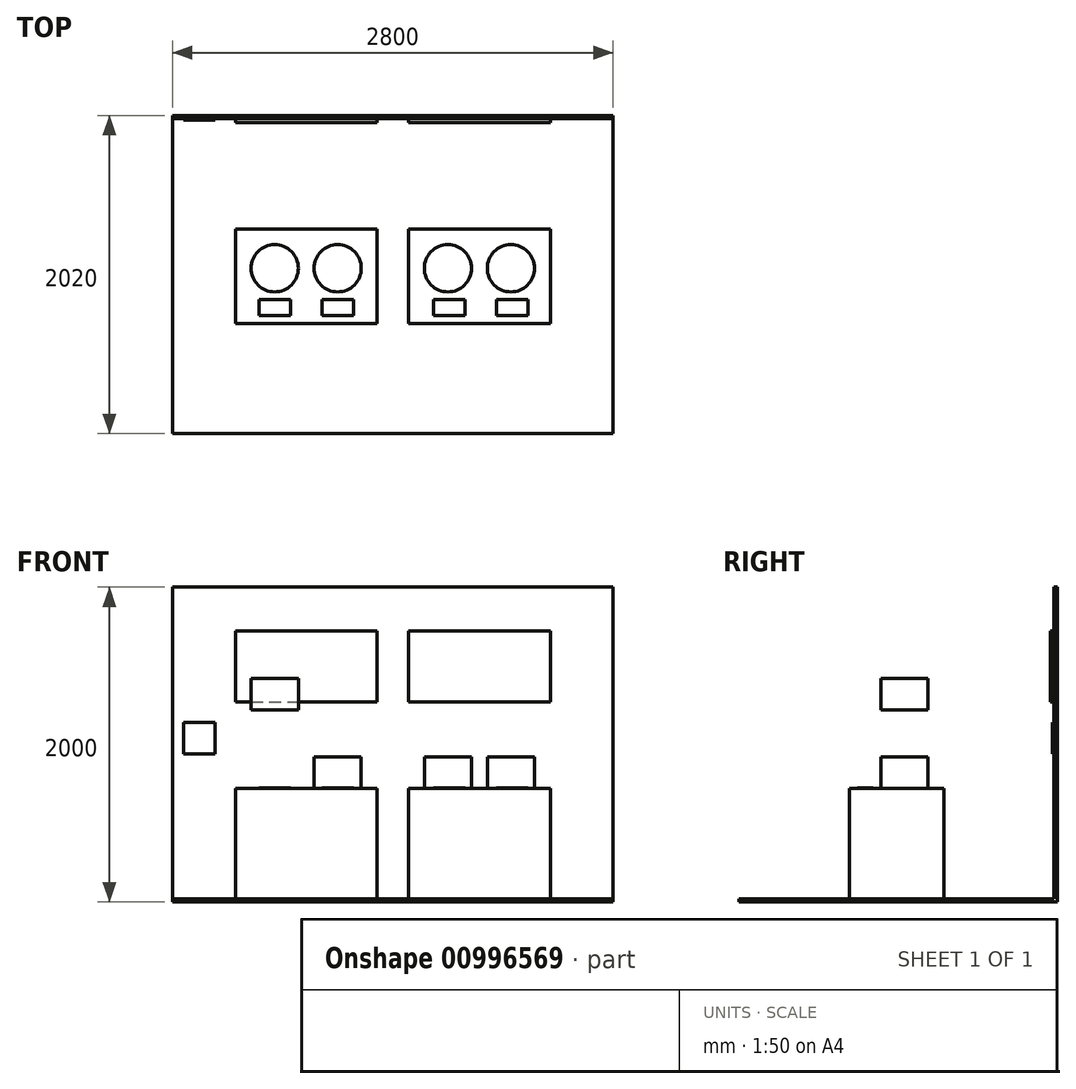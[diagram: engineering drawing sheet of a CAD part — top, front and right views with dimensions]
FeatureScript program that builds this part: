
annotation { "Feature Type Name" : "Feature", "Feature Type Description" : "" }
export const myFeature = defineFeature(function(context is Context, id is Id, definition is map)
    precondition{}
    {
        {
            var Q0;
            Q0=qCreatedBy(makeId("Top.planeOp"),FACE);
            var sketch = newSketch(context, id + "F0", { "sketchPlane" : qUnion([Q0])});
            skLineSegment(sketch, "E0.bottom", {"start": v(-1000, 300) * mm, "end": v(-100, 300) * mm});
            skLineSegment(sketch, "E0.top", {"start": v(-1000, -300) * mm, "end": v(-100, -300) * mm});
            skLineSegment(sketch, "E0.left", {"start": v(-1000, 300) * mm, "end": v(-1000, -300) * mm});
            skLineSegment(sketch, "E0.right", {"start": v(-100, 300) * mm, "end": v(-100, -300) * mm});
            skLineSegment(sketch, "E1.bottom", {"start": v(100, 300) * mm, "end": v(1000, 300) * mm});
            skLineSegment(sketch, "E1.top", {"start": v(100, -300) * mm, "end": v(1000, -300) * mm});
            skLineSegment(sketch, "E1.left", {"start": v(100, 300) * mm, "end": v(100, -300) * mm});
            skLineSegment(sketch, "E1.right", {"start": v(1000, 300) * mm, "end": v(1000, -300) * mm});
            skLineSegment(sketch, "E2", {"start": v(-100, 0) * mm, "end": v(100, 0) * mm, "construction": true});
            skSolve(sketch);
        }
        {
            var Q0;
            Q0 = qSketchRegion(id + "F0", true);
            extrude(context, id + "F1", {"entities" : qUnion([Q0]), "depth" : 700 * mm, "offsetDistance" : 25 * mm});
        }
        {
            var Q0;
            Q0=qCreatedBy(makeId("Top.planeOp"),FACE);
            var sketch = newSketch(context, id + "F2", { "sketchPlane" : qUnion([Q0])});
            skLineSegment(sketch, "E3.bottom", {"start": v(-1400, 1000) * mm, "end": v(1400, 1000) * mm});
            skLineSegment(sketch, "E3.top", {"start": v(-1400, -1000) * mm, "end": v(1400, -1000) * mm});
            skLineSegment(sketch, "E3.left", {"start": v(-1400, 1000) * mm, "end": v(-1400, -1000) * mm});
            skLineSegment(sketch, "E3.right", {"start": v(1400, 1000) * mm, "end": v(1400, -1000) * mm});
            skLineSegment(sketch, "E4", {"start": v(-1400, 1000) * mm, "end": v(1400, -1000) * mm, "construction": true});
            skSolve(sketch);
        }
        {
            var Q0;
            Q0 = qSketchRegion(id + "F2", true);
            extrude(context, id + "F3", {"entities" : qUnion([Q0]), "oppositeDirection" : true, "depth" : 20 * mm, "offsetDistance" : 25 * mm});
        }
        {
            var Q0;
            Q0=makeQuery(id+"F3.opExtrude","SWEPT_FACE",FACE,{"disambiguationData":[OSD([sQuery(id+"F2.wireOp",EDGE,"E3.bottom")])]});
            var sketch = newSketch(context, id + "F4", { "sketchPlane" : qUnion([Q0])});
            skLineSegment(sketch, "E5.bottom", {"start": v(-1400, -20) * mm, "end": v(1400, -20) * mm});
            skLineSegment(sketch, "E5.top", {"start": v(-1400, 1980) * mm, "end": v(1400, 1980) * mm});
            skLineSegment(sketch, "E5.left", {"start": v(-1400, -20) * mm, "end": v(-1400, 1980) * mm});
            skLineSegment(sketch, "E5.right", {"start": v(1400, -20) * mm, "end": v(1400, 1980) * mm});
            skSolve(sketch);
        }
        {
            var Q0;
            Q0 = qSketchRegion(id + "F4", true);
            extrude(context, id + "F5", {"entities" : qUnion([Q0]), "operationType" : NewBodyOperationType.ADD, "depth" : 20 * mm, "offsetDistance" : 25 * mm});
        }
        {
            var Q0;
            Q0=makeQuery(id+"F5.opExtrude","CAP_FACE",FACE,{"disambiguationData":[OSD([sQuery(id+"F4.wireOp",EDGE,"E5.bottom"),sQuery(id+"F4.wireOp",EDGE,"E5.top"),sQuery(id+"F4.wireOp",EDGE,"E5.left"),sQuery(id+"F4.wireOp",EDGE,"E5.right")])],"isStart":true});
            var sketch = newSketch(context, id + "F6", { "sketchPlane" : qUnion([Q0])});
            skLineSegment(sketch, "E6.bottom", {"start": v(-1000, 1700) * mm, "end": v(-100, 1700) * mm});
            skLineSegment(sketch, "E6.top", {"start": v(-1000, 1250) * mm, "end": v(-100, 1250) * mm});
            skLineSegment(sketch, "E6.left", {"start": v(-1000, 1700) * mm, "end": v(-1000, 1250) * mm});
            skLineSegment(sketch, "E6.right", {"start": v(-100, 1700) * mm, "end": v(-100, 1250) * mm});
            skLineSegment(sketch, "E7.1.0.0", {"start": v(100, 1700) * mm, "end": v(1000, 1700) * mm});
            skLineSegment(sketch, "E7.1.0.1", {"start": v(100, 1700) * mm, "end": v(100, 1250) * mm});
            skLineSegment(sketch, "E7.1.0.2", {"start": v(100, 1250) * mm, "end": v(1000, 1250) * mm});
            skLineSegment(sketch, "E7.1.0.3", {"start": v(1000, 1700) * mm, "end": v(1000, 1250) * mm});
            skLineSegment(sketch, "E7.direction1", {"start": v(-1000, 1700) * mm, "end": v(100, 1700) * mm, "construction": true});
            skSolve(sketch);
        }
        {
            var Q0;
            Q0 = qSketchRegion(id + "F6", true);
            extrude(context, id + "F7", {"entities" : qUnion([Q0]), "operationType" : NewBodyOperationType.ADD, "depth" : 25 * mm, "offsetDistance" : 25 * mm});
        }
        {
            var Q0;
            Q0=makeQuery(id+"F1.opExtrude","CAP_FACE",FACE,{"disambiguationData":[OSD([sQuery(id+"F0.wireOp",EDGE,"E0.bottom"),sQuery(id+"F0.wireOp",EDGE,"E0.top"),sQuery(id+"F0.wireOp",EDGE,"E0.left"),sQuery(id+"F0.wireOp",EDGE,"E0.right")])],"isStart":false});
            var sketch = newSketch(context, id + "F8", { "sketchPlane" : qUnion([Q0])});
            skCircle(sketch, "E8", {"center": v(-750, 50) * mm, "radius": 150 * mm});
            skCircle(sketch, "E9.1.0.0", {"center": v(-350, 50) * mm, "radius": 150 * mm});
            skLineSegment(sketch, "E9.direction1", {"start": v(-750, 50) * mm, "end": v(-350, 50) * mm, "construction": true});
            skSolve(sketch);
        }
        {
            var Q0;
            Q0 = qSketchRegion(id + "F8", true);
            extrude(context, id + "F9", {"entities" : qUnion([Q0]), "depth" : 200 * mm, "offsetDistance" : 25 * mm});
        }
        {
            var Q0;
            Q0=makeQuery(id+"F9.opExtrude","SWEPT_BODY",BODY,{"disambiguationData":[OSD([sQuery(id+"F8.wireOp",EDGE,"E9.1.0.0")])]});
            var Q1;
            Q1=makeQuery(id+"F9.opExtrude","SWEPT_BODY",BODY,{"disambiguationData":[OSD([sQuery(id+"F8.wireOp",EDGE,"E8")])]});
            transform(context, id + "F10", {"entities" : qUnion([Q0, Q1]), "transformType" : TransformType.TRANSLATION_3D, "dx" : 1100 * mm, "dy" : 0 * mm, "dz" : 0 * mm, "makeCopy" : true});
        }
        {
            var Q0;
            Q0=makeQuery(id+"F5.opExtrude","CAP_FACE",FACE,{"disambiguationData":[OSD([sQuery(id+"F4.wireOp",EDGE,"E5.bottom"),sQuery(id+"F4.wireOp",EDGE,"E5.top"),sQuery(id+"F4.wireOp",EDGE,"E5.left"),sQuery(id+"F4.wireOp",EDGE,"E5.right")])],"isStart":true});
            var sketch = newSketch(context, id + "F11", { "sketchPlane" : qUnion([Q0])});
            skLineSegment(sketch, "E10.bottom", {"start": v(-1330, 1120) * mm, "end": v(-1130, 1120) * mm});
            skLineSegment(sketch, "E10.top", {"start": v(-1330, 920) * mm, "end": v(-1130, 920) * mm});
            skLineSegment(sketch, "E10.left", {"start": v(-1330, 1120) * mm, "end": v(-1330, 920) * mm});
            skLineSegment(sketch, "E10.right", {"start": v(-1130, 1120) * mm, "end": v(-1130, 920) * mm});
            skSolve(sketch);
        }
        {
            var Q0;
            Q0 = qSketchRegion(id + "F11", true);
            extrude(context, id + "F12", {"entities" : qUnion([Q0]), "operationType" : NewBodyOperationType.ADD, "depth" : 10 * mm, "offsetDistance" : 25 * mm});
        }
        {
            var Q0;
            Q0=makeQuery(id+"F1.opExtrude","CAP_FACE",FACE,{"disambiguationData":[OSD([sQuery(id+"F0.wireOp",EDGE,"E0.bottom"),sQuery(id+"F0.wireOp",EDGE,"E0.top"),sQuery(id+"F0.wireOp",EDGE,"E0.left"),sQuery(id+"F0.wireOp",EDGE,"E0.right")])],"isStart":false});
            var sketch = newSketch(context, id + "F13", { "sketchPlane" : qUnion([Q0])});
            skLineSegment(sketch, "E11.bottom", {"start": v(-850, -150) * mm, "end": v(-650, -150) * mm});
            skLineSegment(sketch, "E11.top", {"start": v(-850, -250) * mm, "end": v(-650, -250) * mm});
            skLineSegment(sketch, "E11.left", {"start": v(-850, -150) * mm, "end": v(-850, -250) * mm});
            skLineSegment(sketch, "E11.right", {"start": v(-650, -150) * mm, "end": v(-650, -250) * mm});
            skLineSegment(sketch, "E12", {"start": v(-750, -150) * mm, "end": v(-750, 50) * mm, "construction": true});
            skLineSegment(sketch, "E13.1.0.0", {"start": v(-450, -150) * mm, "end": v(-250, -150) * mm});
            skLineSegment(sketch, "E13.1.0.1", {"start": v(-450, -150) * mm, "end": v(-450, -250) * mm});
            skLineSegment(sketch, "E13.1.0.2", {"start": v(-450, -250) * mm, "end": v(-250, -250) * mm});
            skLineSegment(sketch, "E13.1.0.3", {"start": v(-250, -150) * mm, "end": v(-250, -250) * mm});
            skLineSegment(sketch, "E13.1.0.4", {"start": v(-350, -150) * mm, "end": v(-350, 50) * mm, "construction": true});
            skLineSegment(sketch, "E13.direction1", {"start": v(-850, -150) * mm, "end": v(-450, -150) * mm, "construction": true});
            skSolve(sketch);
        }
        {
            var Q0;
            Q0 = qSketchRegion(id + "F13", true);
            extrude(context, id + "F14", {"entities" : qUnion([Q0]), "depth" : 5 * mm, "offsetDistance" : 25 * mm});
        }
        {
            var Q0;
            Q0=makeQuery(id+"F14.opExtrude","SWEPT_BODY",BODY,{"disambiguationData":[OSD([sQuery(id+"F13.wireOp",EDGE,"E13.1.0.0"),sQuery(id+"F13.wireOp",EDGE,"E13.1.0.1"),sQuery(id+"F13.wireOp",EDGE,"E13.1.0.2"),sQuery(id+"F13.wireOp",EDGE,"E13.1.0.3")])]});
            var Q1;
            Q1=makeQuery(id+"F14.opExtrude","SWEPT_BODY",BODY,{"disambiguationData":[OSD([sQuery(id+"F13.wireOp",EDGE,"E11.bottom"),sQuery(id+"F13.wireOp",EDGE,"E11.top"),sQuery(id+"F13.wireOp",EDGE,"E11.left"),sQuery(id+"F13.wireOp",EDGE,"E11.right")])]});
            transform(context, id + "F15", {"entities" : qUnion([Q0, Q1]), "transformType" : TransformType.TRANSLATION_3D, "dx" : 1110 * mm, "dy" : 0 * mm, "dz" : 0 * mm, "makeCopy" : true});
        }
        {
            var Q0;
            Q0=makeQuery(id+"F9.opExtrude","SWEPT_BODY",BODY,{"disambiguationData":[OSD([sQuery(id+"F8.wireOp",EDGE,"E8")])]});
            transform(context, id + "F16", {"entities" : qUnion([Q0]), "transformType" : TransformType.TRANSLATION_3D, "dx" : 0 * mm, "dy" : 0 * mm, "dz" : 500 * mm, "makeCopy" : false});
        }
    });
